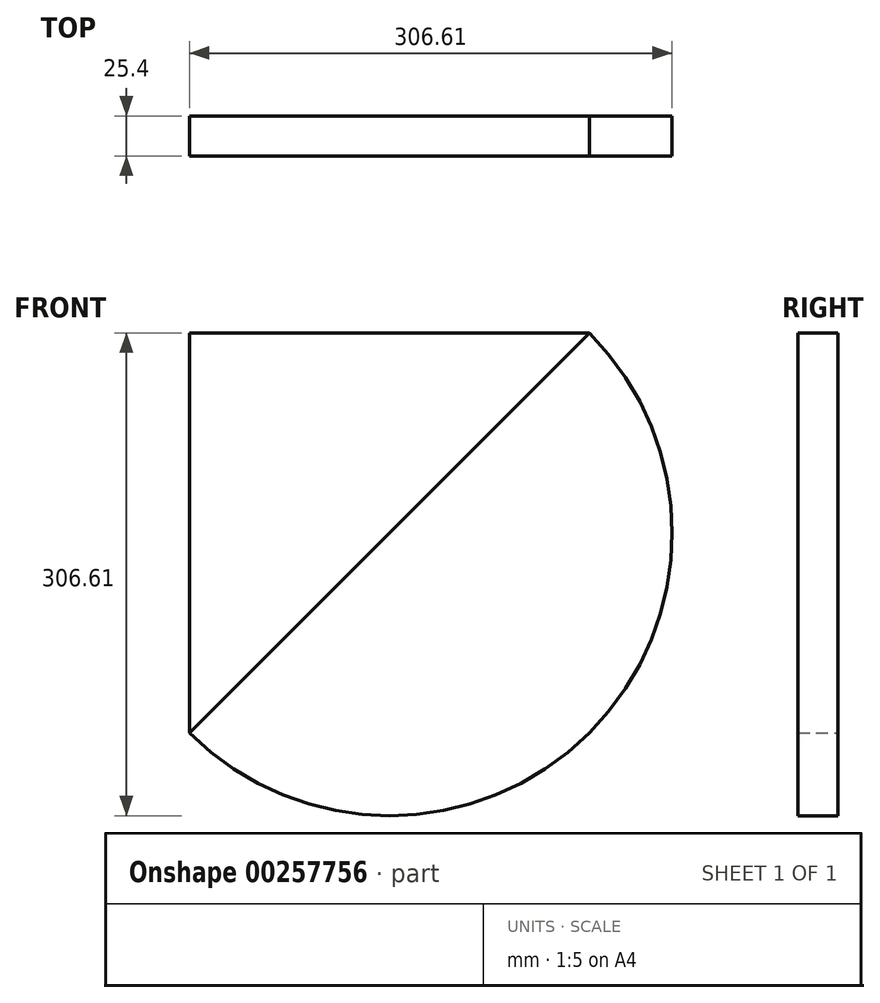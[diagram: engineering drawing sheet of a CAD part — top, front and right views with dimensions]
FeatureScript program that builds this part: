
annotation { "Feature Type Name" : "Feature", "Feature Type Description" : "" }
export const myFeature = defineFeature(function(context is Context, id is Id, definition is map)
    precondition{}
    {
        {
            var Q0;
            Q0=qCreatedBy(makeId("Front.planeOp"),FACE);
            var sketch = newSketch(context, id + "F0", { "sketchPlane" : qUnion([Q0])});
            skLineSegment(sketch, "E0.bottom", {"start": v(127, 127) * mm, "end": v(-127, 127) * mm});
            skLineSegment(sketch, "E0.right", {"start": v(-127, 127) * mm, "end": v(-127, -127) * mm});
            skPoint(sketch, "E0.middle", {"position": v(0, 0) * mm});
            skLineSegment(sketch, "E1", {"start": v(-127, -127) * mm, "end": v(127, 127) * mm});
            skPoint(sketch, "E0.top.start.orphan", {"position": v(127, -127) * mm});
            skArc(sketch, "E2", {"start": v(127, 127) * mm, "mid": v(127, -127) * mm, "end": v(-127, -127) * mm});
            skSolve(sketch);
        }
        {
            var Q0;
            Q0=makeQuery(id+"F0.imprint","IMPRINT",FACE,{"disambiguationData":[TD([[makeQuery(id+"F0.imprint","IMPRINT",EDGE,{"derivedFrom":sQuery(id+"F0.wireOp",EDGE,"E0.bottom")}),1.0]])]});
            extrude(context, id + "F1", {"entities" : qUnion([Q0]), "depth" : 25.4 * mm});
        }
        {
            var Q0;
            Q0=makeQuery(id+"F0.imprint","IMPRINT",FACE,{"disambiguationData":[TD([[makeQuery(id+"F0.imprint","IMPRINT",EDGE,{"derivedFrom":sQuery(id+"F0.wireOp",EDGE,"E1")}),-1.0]])]});
            extrude(context, id + "F2", {"entities" : qUnion([Q0]), "depth" : 25.4 * mm});
        }
    });
